# Revit family: ASL_Designline_Skirting_Wall_Starter_64mm Stud_2x13mm Gib_BS
name_source: partatom
category: Detail Items
revit_build: Autodesk Revit 2018 (Build: 20170223_1515(x64)
units: mm (PartAtom-declared; Revit-internal decimal feet)

## family parameters
Rotate with component = No
Section Shape = Not Defined
Shared = Yes

## types (3) — shared parameters
Manufacturer = Aluminate Solutions Limited
Technical Info = www.aluminate.nz

## per-type parameters (varying)
| type | Type Comments |
| Skirting 100mm | ASL Designline Wall Starter With 100mm Skirting for ASL 420 Headsection 64mm 2xStud 13mm Gib Bothside Wall |
| Skirting 120mm | ASL Designline Wall Starter With 120mm Skirting for ASL 420 Headsection 64mm 2xStud 13mm Gib Bothside Wall |
| Skirting 150mm | ASL Designline Wall Starter With 150mm Skirting for ASL 420 Headsection 64mm 2xStud 13mm Gib Bothside Wall |

type visibility flags: 3 boolean params named "<type name>" — each type sets only its own to Yes (folded from table)

## geometry (parser evidence)
native form markers: Sweep x4
no freeform markers — native parametric forms only
